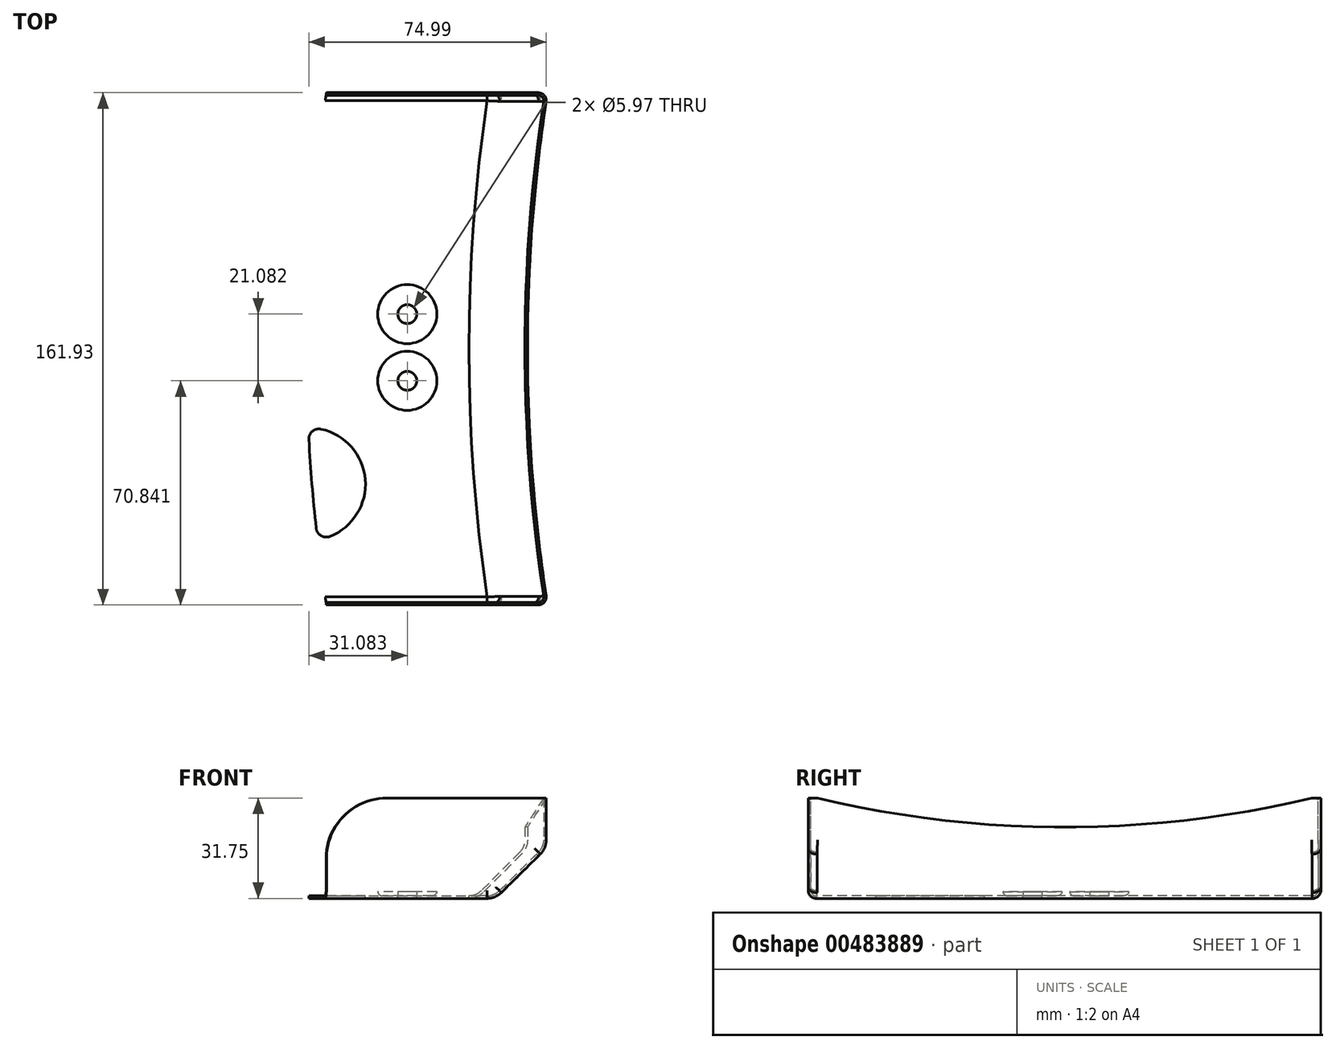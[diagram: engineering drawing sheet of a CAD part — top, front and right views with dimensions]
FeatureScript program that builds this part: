
annotation { "Feature Type Name" : "Feature", "Feature Type Description" : "" }
export const myFeature = defineFeature(function(context is Context, id is Id, definition is map)
    precondition{}
    {
        {
            var Q0;
            Q0=qCreatedBy(makeId("Top.planeOp"),FACE);
            var sketch = newSketch(context, id + "F0", { "sketchPlane" : qUnion([Q0])});
            skLineSegment(sketch, "E0.bottom", {"start": v(0, 0) * mm, "end": v(69.85, 0) * mm});
            skLineSegment(sketch, "E0.top", {"start": v(0, 161.93) * mm, "end": v(69.85, 161.93) * mm});
            skLineSegment(sketch, "E0.left", {"start": v(0, 0) * mm, "end": v(0, 161.93) * mm, "construction": true});
            skLineSegment(sketch, "E0.right", {"start": v(69.85, 0) * mm, "end": v(69.85, 161.93) * mm, "construction": true});
            skArc(sketch, "E1", {"start": v(0, 161.92) * mm, "mid": v(-6.35, 80.96) * mm, "end": v(0, 0) * mm});
            skArc(sketch, "E2", {"start": v(69.85, 161.92) * mm, "mid": v(63.5, 80.96) * mm, "end": v(69.85, 0) * mm});
            skSolve(sketch);
        }
        {
            var Q0;
            Q0=makeQuery(id+"F0.imprint","IMPRINT",FACE,{"disambiguationData":[TD([[makeQuery(id+"F0.imprint","IMPRINT",EDGE,{"derivedFrom":sQuery(id+"F0.wireOp",EDGE,"E0.bottom")}),1.0]])]});
            var Q1;
            Q1 = qBodyType(qCreatedBy(id + "F0" ,EDGE), BodyType.WIRE);
            extrude(context, id + "F1", {"entities" : qUnion([Q0]), "surfaceEntities" : qUnion([Q1]), "depth" : 31.75 * mm});
        }
        {
            var Q0;
            Q0=makeQuery(id+"F1.opExtrude","CAP_EDGE",EDGE,{"disambiguationData":[OSD([sQuery(id+"F0.wireOp",EDGE,"E2")])],"isStart":true});
            chamfer(context, id + "F2", {"entities" : qUnion([Q0]), "width" : 15.88 * mm, "tangentPropagation" : true});
        }
        {
            var Q0;
            Q0=makeQuery(id+"F1.opExtrude","CAP_EDGE",EDGE,{"disambiguationData":[OSD([sQuery(id+"F0.wireOp",EDGE,"E1")])],"isStart":false});
            fillet(context, id + "F3", {"entities" : qUnion([Q0]), "radius" : 19.05 * mm, "tangentPropagation" : true, "allowEdgeOverflow" : false});
        }
        {
            var Q0;
            {var subQ0=sQuery(id+"F0.wireOp",EDGE,"E2");Q0=makeQuery(id+"F2.opChamfer","BLEND_EDGE",EDGE,{"blendedFrom":[makeQuery(id+"F1.opExtrude","CAP_EDGE",EDGE,{"disambiguationData":[OSD([subQ0])],"isStart":true}),makeQuery(id+"F1.opExtrude","SWEPT_FACE",FACE,{"disambiguationData":[OSD([subQ0])]})],"blendedInto":[makeQuery(id+"F1.opExtrude","SWEPT_FACE",FACE,{"disambiguationData":[OSD([subQ0])]})]});}
            var Q1;
            {var subQ0=sQuery(id+"F0.wireOp",EDGE,"E2");Q1=makeQuery(id+"F2.opChamfer","BLEND_EDGE",EDGE,{"blendedFrom":[makeQuery(id+"F1.opExtrude","CAP_EDGE",EDGE,{"disambiguationData":[OSD([subQ0])],"isStart":true}),makeQuery(id+"F1.opExtrude","CAP_FACE",FACE,{"disambiguationData":[OSD([sQuery(id+"F0.wireOp",EDGE,"E0.bottom"),sQuery(id+"F0.wireOp",EDGE,"E0.top"),sQuery(id+"F0.wireOp",EDGE,"E1"),subQ0])],"isStart":true})],"blendedInto":[makeQuery(id+"F1.opExtrude","CAP_FACE",FACE,{"disambiguationData":[OSD([sQuery(id+"F0.wireOp",EDGE,"E0.bottom"),sQuery(id+"F0.wireOp",EDGE,"E0.top"),sQuery(id+"F0.wireOp",EDGE,"E1"),subQ0])],"isStart":true})]});}
            fillet(context, id + "F4", {"entities" : qUnion([Q0, Q1]), "radius" : 6.35 * mm, "tangentPropagation" : true, "allowEdgeOverflow" : false});
        }
        {
            var Q0;
            Q0=makeQuery(id+"F1.opExtrude","SWEPT_EDGE",EDGE,{"disambiguationData":[OSD([sQuery(id+"F0.wireOp",EDGE,"E0.top"),sQuery(id+"F0.wireOp",EDGE,"E2")])]});
            var Q1;
            {var subQ0=sQuery(id+"F0.wireOp",EDGE,"E2");Q1=makeQuery(id+"F4.opFillet","BLEND_EDGE",EDGE,{"blendedFrom":[makeQuery(id+"F2.opChamfer","BLEND_EDGE",EDGE,{"blendedFrom":[makeQuery(id+"F1.opExtrude","CAP_EDGE",EDGE,{"disambiguationData":[OSD([subQ0])],"isStart":true}),makeQuery(id+"F1.opExtrude","SWEPT_FACE",FACE,{"disambiguationData":[OSD([subQ0])]})],"blendedInto":[makeQuery(id+"F1.opExtrude","SWEPT_FACE",FACE,{"disambiguationData":[OSD([subQ0])]})]}),makeQuery(id+"F1.opExtrude","SWEPT_FACE",FACE,{"disambiguationData":[OSD([sQuery(id+"F0.wireOp",EDGE,"E0.bottom")])]})],"blendedInto":[makeQuery(id+"F1.opExtrude","SWEPT_FACE",FACE,{"disambiguationData":[OSD([sQuery(id+"F0.wireOp",EDGE,"E0.bottom")])]})]});}
            var Q2;
            Q2=makeQuery(id+"F1.opExtrude","SWEPT_EDGE",EDGE,{"disambiguationData":[OSD([sQuery(id+"F0.wireOp",EDGE,"E0.bottom"),sQuery(id+"F0.wireOp",EDGE,"E2")])]});
            var Q3;
            Q3=makeQuery(id+"F2.opChamfer","BLEND_EDGE",EDGE,{"blendedFrom":[makeQuery(id+"F1.opExtrude","CAP_EDGE",EDGE,{"disambiguationData":[OSD([sQuery(id+"F0.wireOp",EDGE,"E2")])],"isStart":true}),makeQuery(id+"F1.opExtrude","SWEPT_FACE",FACE,{"disambiguationData":[OSD([sQuery(id+"F0.wireOp",EDGE,"E0.top")])]})],"blendedInto":[makeQuery(id+"F1.opExtrude","SWEPT_FACE",FACE,{"disambiguationData":[OSD([sQuery(id+"F0.wireOp",EDGE,"E0.top")])]})]});
            var Q4;
            Q4=makeQuery(id+"F2.opChamfer","BLEND_EDGE",EDGE,{"blendedFrom":[makeQuery(id+"F1.opExtrude","CAP_EDGE",EDGE,{"disambiguationData":[OSD([sQuery(id+"F0.wireOp",EDGE,"E2")])],"isStart":true}),makeQuery(id+"F1.opExtrude","SWEPT_FACE",FACE,{"disambiguationData":[OSD([sQuery(id+"F0.wireOp",EDGE,"E0.bottom")])]})],"blendedInto":[makeQuery(id+"F1.opExtrude","SWEPT_FACE",FACE,{"disambiguationData":[OSD([sQuery(id+"F0.wireOp",EDGE,"E0.bottom")])]})]});
            var Q5;
            {var subQ0=sQuery(id+"F0.wireOp",EDGE,"E0.top");var subQ1=sQuery(id+"F0.wireOp",EDGE,"E2");Q5=makeQuery(id+"F4.opFillet","BLEND_EDGE",EDGE,{"blendedFrom":[makeQuery(id+"F2.opChamfer","BLEND_EDGE",EDGE,{"blendedFrom":[makeQuery(id+"F1.opExtrude","CAP_EDGE",EDGE,{"disambiguationData":[OSD([subQ1])],"isStart":true}),makeQuery(id+"F1.opExtrude","CAP_FACE",FACE,{"disambiguationData":[OSD([sQuery(id+"F0.wireOp",EDGE,"E0.bottom"),subQ0,sQuery(id+"F0.wireOp",EDGE,"E1"),subQ1])],"isStart":true})],"blendedInto":[makeQuery(id+"F1.opExtrude","CAP_FACE",FACE,{"disambiguationData":[OSD([sQuery(id+"F0.wireOp",EDGE,"E0.bottom"),subQ0,sQuery(id+"F0.wireOp",EDGE,"E1"),subQ1])],"isStart":true})]}),makeQuery(id+"F1.opExtrude","SWEPT_FACE",FACE,{"disambiguationData":[OSD([subQ0])]})],"blendedInto":[makeQuery(id+"F1.opExtrude","SWEPT_FACE",FACE,{"disambiguationData":[OSD([subQ0])]})]});}
            var Q6;
            Q6=makeQuery(id+"F1.opExtrude","CAP_EDGE",EDGE,{"disambiguationData":[OSD([sQuery(id+"F0.wireOp",EDGE,"E0.top")])],"isStart":true});
            var Q7;
            {var subQ0=sQuery(id+"F0.wireOp",EDGE,"E2");Q7=makeQuery(id+"F4.opFillet","BLEND_EDGE",EDGE,{"blendedFrom":[makeQuery(id+"F2.opChamfer","BLEND_EDGE",EDGE,{"blendedFrom":[makeQuery(id+"F1.opExtrude","CAP_EDGE",EDGE,{"disambiguationData":[OSD([subQ0])],"isStart":true}),makeQuery(id+"F1.opExtrude","SWEPT_FACE",FACE,{"disambiguationData":[OSD([subQ0])]})],"blendedInto":[makeQuery(id+"F1.opExtrude","SWEPT_FACE",FACE,{"disambiguationData":[OSD([subQ0])]})]}),makeQuery(id+"F1.opExtrude","SWEPT_FACE",FACE,{"disambiguationData":[OSD([sQuery(id+"F0.wireOp",EDGE,"E0.top")])]})],"blendedInto":[makeQuery(id+"F1.opExtrude","SWEPT_FACE",FACE,{"disambiguationData":[OSD([sQuery(id+"F0.wireOp",EDGE,"E0.top")])]})]});}
            var Q8;
            {var subQ0=sQuery(id+"F0.wireOp",EDGE,"E0.bottom");var subQ1=sQuery(id+"F0.wireOp",EDGE,"E2");Q8=makeQuery(id+"F4.opFillet","BLEND_EDGE",EDGE,{"blendedFrom":[makeQuery(id+"F2.opChamfer","BLEND_EDGE",EDGE,{"blendedFrom":[makeQuery(id+"F1.opExtrude","CAP_EDGE",EDGE,{"disambiguationData":[OSD([subQ1])],"isStart":true}),makeQuery(id+"F1.opExtrude","CAP_FACE",FACE,{"disambiguationData":[OSD([subQ0,sQuery(id+"F0.wireOp",EDGE,"E0.top"),sQuery(id+"F0.wireOp",EDGE,"E1"),subQ1])],"isStart":true})],"blendedInto":[makeQuery(id+"F1.opExtrude","CAP_FACE",FACE,{"disambiguationData":[OSD([subQ0,sQuery(id+"F0.wireOp",EDGE,"E0.top"),sQuery(id+"F0.wireOp",EDGE,"E1"),subQ1])],"isStart":true})]}),makeQuery(id+"F1.opExtrude","SWEPT_FACE",FACE,{"disambiguationData":[OSD([subQ0])]})],"blendedInto":[makeQuery(id+"F1.opExtrude","SWEPT_FACE",FACE,{"disambiguationData":[OSD([subQ0])]})]});}
            var Q9;
            Q9=makeQuery(id+"F1.opExtrude","CAP_EDGE",EDGE,{"disambiguationData":[OSD([sQuery(id+"F0.wireOp",EDGE,"E0.bottom")])],"isStart":true});
            fillet(context, id + "F5", {"entities" : qUnion([Q0, Q1, Q2, Q3, Q4, Q5, Q6, Q7, Q8, Q9]), "radius" : 2.54 * mm, "tangentPropagation" : true, "allowEdgeOverflow" : false});
        }
        {
            var Q0;
            Q0=makeQuery(id+"F1.opExtrude","CAP_FACE",FACE,{"disambiguationData":[OSD([sQuery(id+"F0.wireOp",EDGE,"E0.bottom"),sQuery(id+"F0.wireOp",EDGE,"E0.top"),sQuery(id+"F0.wireOp",EDGE,"E1"),sQuery(id+"F0.wireOp",EDGE,"E2")])],"isStart":false});
            shell(context, id + "F6", {"entities" : qUnion([Q0]), "thickness" : 0.81 * mm});
        }
        {
            var Q0;
            Q0=qCreatedBy(makeId("Right.planeOp"),FACE);
            var sketch = newSketch(context, id + "F7", { "sketchPlane" : qUnion([Q0])});
            skFitSpline(sketch, "E3.0", {"points": [v(0.81, 31.75) * mm, v(0.81, 25.4) * mm, v(0.81, 19.05) * mm, v(0.81, 12.7) * mm]});
            skFitSpline(sketch, "E3.1", {"points": [v(161.11, 12.7) * mm, v(161.11, 19.05) * mm, v(161.11, 25.4) * mm, v(161.11, 31.75) * mm]});
            skLineSegment(sketch, "E3.2", {"start": v(161.11, 12.7) * mm, "end": v(161.11, 2.54) * mm});
            skLineSegment(sketch, "E3.3", {"start": v(159.38, 0.81) * mm, "end": v(2.54, 0.81) * mm});
            skLineSegment(sketch, "E3.4", {"start": v(0.81, 12.7) * mm, "end": v(0.81, 2.54) * mm});
            skLineSegment(sketch, "E4", {"start": v(161.11, 31.75) * mm, "end": v(0.81, 31.75) * mm});
            skPoint(sketch, "E5.visualSharp", {"position": v(161.11, 0.81) * mm});
            skArc(sketch, "E5.filletArc", {"start": v(159.38, 0.81) * mm, "mid": v(160.6, 1.32) * mm, "end": v(161.11, 2.54) * mm});
            skPoint(sketch, "E6.visualSharp", {"position": v(0.81, 0.81) * mm});
            skArc(sketch, "E6.filletArc", {"start": v(0.81, 2.54) * mm, "mid": v(1.32, 1.32) * mm, "end": v(2.54, 0.81) * mm});
            skSolve(sketch);
        }
        {
            var Q0;
            Q0 = qSketchRegion(id + "F7", true);
            extrude(context, id + "F8", {"entities" : qUnion([Q0]), "operationType" : NewBodyOperationType.REMOVE, "oppositeDirection" : true, "depth" : 46.06 * mm, "hasSecondDirection" : true, "secondDirectionOppositeDirection" : false, "secondDirectionDepth" : 24.57 * mm});
        }
        {
            var Q0;
            Q0=qCreatedBy(makeId("Right.planeOp"),FACE);
            var sketch = newSketch(context, id + "F9", { "sketchPlane" : qUnion([Q0])});
            skLineSegment(sketch, "E7.0", {"start": v(2.8, 31.75) * mm, "end": v(2.8, 18.5) * mm, "construction": true});
            skLineSegment(sketch, "E8.0", {"start": v(159.13, 18.5) * mm, "end": v(159.13, 31.75) * mm, "construction": true});
            skArc(sketch, "E9", {"start": v(2.8, 31.75) * mm, "mid": v(80.96, 22.52) * mm, "end": v(159.13, 31.75) * mm});
            skLineSegment(sketch, "E10", {"start": v(159.13, 31.75) * mm, "end": v(2.8, 31.75) * mm});
            skSolve(sketch);
        }
        {
            var Q0;
            Q0=makeQuery(id+"F9.imprint","IMPRINT",FACE,{"disambiguationData":[TD([[makeQuery(id+"F9.imprint","IMPRINT",EDGE,{"derivedFrom":sQuery(id+"F9.wireOp",EDGE,"E9")}),1.0]])]});
            extrude(context, id + "F10", {"entities" : qUnion([Q0]), "operationType" : NewBodyOperationType.REMOVE, "endBound" : BoundingType.THROUGH_ALL, "depth" : 25.4 * mm});
        }
        {
            var Q0;
            {var subQ0=sQuery(id+"F0.wireOp",EDGE,"E2");var subQ1=sQuery(id+"F0.wireOp",EDGE,"E1");var subQ2=sQuery(id+"F0.wireOp",EDGE,"E0.top");var subQ3=sQuery(id+"F0.wireOp",EDGE,"E0.bottom");Q0=makeQuery(id+"F6.opShell","OFFSET_FACE",FACE,{"disambiguationData":[OSD([subQ3,subQ2,subQ1,subQ0]),TDD([makeQuery(id+"F1.opExtrude","CAP_FACE",FACE,{"disambiguationData":[OSD([subQ3,subQ2,subQ1,subQ0])],"isStart":true})])]});}
            var sketch = newSketch(context, id + "F11", { "sketchPlane" : qUnion([Q0])});
            skLineSegment(sketch, "E11", {"start": v(-5.95, 81.38) * mm, "end": v(45, 81.38) * mm, "construction": true});
            skFitSpline(sketch, "E12.0", {"points": [v(0.34, 0.4) * mm, v(10.8, 0.4) * mm, v(21.24, 0.4) * mm, v(31.7, 0.4) * mm], "construction": true});
            skFitSpline(sketch, "E13.0", {"points": [v(31.7, 161.53) * mm, v(21.24, 161.53) * mm, v(10.8, 161.53) * mm, v(0.34, 161.53) * mm], "construction": true});
            skLineSegment(sketch, "E14.0", {"start": v(-5.33, 106.78) * mm, "end": v(25.94, 106.78) * mm, "construction": true});
            skLineSegment(sketch, "E15.0", {"start": v(5.53, 138.53) * mm, "end": v(25.94, 138.53) * mm, "construction": true});
            skArc(sketch, "E16", {"start": v(-5.33, 106.78) * mm, "mid": v(11.36, 118.8) * mm, "end": v(5.53, 138.53) * mm});
            skArc(sketch, "E17", {"start": v(5.53, 138.53) * mm, "mid": v(-22.29, 130.32) * mm, "end": v(-5.33, 106.78) * mm});
            skArc(sketch, "E18.MirrorCS", {"start": v(5.53, 24.23) * mm, "mid": v(-22.29, 32.45) * mm, "end": v(-5.33, 55.98) * mm});
            skArc(sketch, "E19.MirrorCS", {"start": v(-5.33, 55.98) * mm, "mid": v(11.36, 43.96) * mm, "end": v(5.53, 24.23) * mm});
            skCircle(sketch, "E20", {"center": v(25.52, 91.92) * mm, "radius": 2.98 * mm});
            skCircle(sketch, "E21.MirrorC", {"center": v(25.52, 70.84) * mm, "radius": 2.98 * mm});
            skSolve(sketch);
        }
        {
            var Q0;
            {var subQ0=sQuery(id+"F11.wireOp",EDGE,"E16");Q0=makeQuery(id+"F11.imprint","IMPRINT",FACE,{"disambiguationData":[TD([[makeQuery(id+"F11.imprint","IMPRINT",EDGE,{"derivedFrom":subQ0}),1.0]])]});}
            var Q1;
            {var subQ0=sQuery(id+"F11.wireOp",EDGE,"E17");Q1=makeQuery(id+"F11.imprint","IMPRINT",FACE,{"disambiguationData":[TD([[makeQuery(id+"F11.imprint","IMPRINT",EDGE,{"derivedFrom":subQ0}),1.0]])]});}
            var Q2;
            {var subQ0=sQuery(id+"F11.wireOp",EDGE,"E18.MirrorCS");Q2=makeQuery(id+"F11.imprint","IMPRINT",FACE,{"disambiguationData":[TD([[makeQuery(id+"F11.imprint","IMPRINT",EDGE,{"derivedFrom":subQ0}),-1.0]])]});}
            var Q3;
            {var subQ0=sQuery(id+"F11.wireOp",EDGE,"E19.MirrorCS");Q3=makeQuery(id+"F11.imprint","IMPRINT",FACE,{"disambiguationData":[TD([[makeQuery(id+"F11.imprint","IMPRINT",EDGE,{"derivedFrom":subQ0}),-1.0]])]});}
            var Q4;
            {var subQ0=sQuery(id+"F11.wireOp",EDGE,"E20");var subQ1=sQuery(id+"F0.wireOp",EDGE,"E2");var subQ2=sQuery(id+"F0.wireOp",EDGE,"E1");var subQ3=sQuery(id+"F0.wireOp",EDGE,"E0.top");var subQ4=sQuery(id+"F0.wireOp",EDGE,"E0.bottom");var subQ5=makeQuery(id+"F1.opExtrude","CAP_FACE",FACE,{"disambiguationData":[OSD([subQ4,subQ3,subQ2,subQ1])],"isStart":true});var subQ6=makeQuery(id+"F6.opShell","OFFSET_EDGE",EDGE,{"disambiguationData":[OSD([subQ4,subQ3,subQ2,subQ1]),TDD([makeQuery(id+"F4.opFillet","BLEND_EDGE",EDGE,{"blendedFrom":[makeQuery(id+"F2.opChamfer","BLEND_EDGE",EDGE,{"blendedFrom":[makeQuery(id+"F1.opExtrude","CAP_EDGE",EDGE,{"disambiguationData":[OSD([subQ1])],"isStart":true}),subQ5],"blendedInto":[subQ5]}),subQ5],"blendedInto":[subQ5]})])]});var subQ7=makeQuery(id+"F11.imprint","INTERSECT",VERTEX,{"disambiguationData":[OD(0.0)],"derivedFrom":[subQ6,subQ0]});Q4=makeQuery(id+"F11.imprint","IMPRINT",FACE,{"disambiguationData":[TD([[makeQuery(id+"F11.imprint","IMPRINT",EDGE,{"disambiguationData":[TD([[subQ7,-1.0]])],"derivedFrom":subQ0}),1.0]])]});}
            var Q5;
            {var subQ0=sQuery(id+"F11.wireOp",EDGE,"E21.MirrorC");var subQ1=sQuery(id+"F0.wireOp",EDGE,"E2");var subQ2=sQuery(id+"F0.wireOp",EDGE,"E1");var subQ3=sQuery(id+"F0.wireOp",EDGE,"E0.top");var subQ4=sQuery(id+"F0.wireOp",EDGE,"E0.bottom");var subQ5=makeQuery(id+"F1.opExtrude","CAP_FACE",FACE,{"disambiguationData":[OSD([subQ4,subQ3,subQ2,subQ1])],"isStart":true});var subQ6=makeQuery(id+"F6.opShell","OFFSET_EDGE",EDGE,{"disambiguationData":[OSD([subQ4,subQ3,subQ2,subQ1]),TDD([makeQuery(id+"F4.opFillet","BLEND_EDGE",EDGE,{"blendedFrom":[makeQuery(id+"F2.opChamfer","BLEND_EDGE",EDGE,{"blendedFrom":[makeQuery(id+"F1.opExtrude","CAP_EDGE",EDGE,{"disambiguationData":[OSD([subQ1])],"isStart":true}),subQ5],"blendedInto":[subQ5]}),subQ5],"blendedInto":[subQ5]})])]});var subQ7=makeQuery(id+"F11.imprint","INTERSECT",VERTEX,{"disambiguationData":[OD(0.0)],"derivedFrom":[subQ6,subQ0]});Q5=makeQuery(id+"F11.imprint","IMPRINT",FACE,{"disambiguationData":[TD([[makeQuery(id+"F11.imprint","IMPRINT",EDGE,{"disambiguationData":[TD([[subQ7,-1.0]])],"derivedFrom":subQ0}),-1.0]])]});}
            extrude(context, id + "F12", {"entities" : qUnion([Q0, Q1, Q2, Q3, Q4, Q5]), "operationType" : NewBodyOperationType.REMOVE, "oppositeDirection" : true, "depth" : 25.4 * mm});
        }
        {
            var Q0;
            {var subQ0=sQuery(id+"F11.wireOp",EDGE,"E17");var subQ1=sQuery(id+"F7.wireOp",EDGE,"E3.3");var subQ2=sQuery(id+"F0.wireOp",EDGE,"E1");Q0=makeQuery(id+"F12.boolean.opBoolean","COPY",EDGE,{"derivedFrom":makeQuery(id+"F12.opExtrude","SWEPT_EDGE",EDGE,{"disambiguationData":[OSD([subQ2,subQ1,subQ0]),TDD([makeQuery(id+"F11.imprint","INTERSECT",VERTEX,{"disambiguationData":[OD(1.0)],"derivedFrom":[makeQuery(id+"F8.boolean.opBoolean","INTERSECT",EDGE,{"derivedFrom":[makeQuery(id+"F1.opExtrude","SWEPT_FACE",FACE,{"disambiguationData":[OSD([subQ2])]}),makeQuery(id+"F8.opExtrude","SWEPT_FACE",FACE,{"disambiguationData":[OSD([subQ1])]})]}),subQ0]})])]})});}
            var Q1;
            {var subQ0=sQuery(id+"F11.wireOp",EDGE,"E17");var subQ1=sQuery(id+"F7.wireOp",EDGE,"E3.3");var subQ2=sQuery(id+"F0.wireOp",EDGE,"E1");Q1=makeQuery(id+"F12.boolean.opBoolean","COPY",EDGE,{"derivedFrom":makeQuery(id+"F12.opExtrude","SWEPT_EDGE",EDGE,{"disambiguationData":[OSD([subQ2,subQ1,subQ0]),TDD([makeQuery(id+"F11.imprint","INTERSECT",VERTEX,{"disambiguationData":[OD(0.0)],"derivedFrom":[makeQuery(id+"F8.boolean.opBoolean","INTERSECT",EDGE,{"derivedFrom":[makeQuery(id+"F1.opExtrude","SWEPT_FACE",FACE,{"disambiguationData":[OSD([subQ2])]}),makeQuery(id+"F8.opExtrude","SWEPT_FACE",FACE,{"disambiguationData":[OSD([subQ1])]})]}),subQ0]})])]})});}
            var Q2;
            {var subQ0=sQuery(id+"F11.wireOp",EDGE,"E18.MirrorCS");var subQ1=sQuery(id+"F7.wireOp",EDGE,"E3.3");var subQ2=sQuery(id+"F0.wireOp",EDGE,"E1");Q2=makeQuery(id+"F12.boolean.opBoolean","COPY",EDGE,{"derivedFrom":makeQuery(id+"F12.opExtrude","SWEPT_EDGE",EDGE,{"disambiguationData":[OSD([subQ2,subQ1,subQ0]),TDD([makeQuery(id+"F11.imprint","INTERSECT",VERTEX,{"disambiguationData":[OD(1.0)],"derivedFrom":[makeQuery(id+"F8.boolean.opBoolean","INTERSECT",EDGE,{"derivedFrom":[makeQuery(id+"F1.opExtrude","SWEPT_FACE",FACE,{"disambiguationData":[OSD([subQ2])]}),makeQuery(id+"F8.opExtrude","SWEPT_FACE",FACE,{"disambiguationData":[OSD([subQ1])]})]}),subQ0]})])]})});}
            var Q3;
            {var subQ0=sQuery(id+"F11.wireOp",EDGE,"E18.MirrorCS");var subQ1=sQuery(id+"F7.wireOp",EDGE,"E3.3");var subQ2=sQuery(id+"F0.wireOp",EDGE,"E1");Q3=makeQuery(id+"F12.boolean.opBoolean","COPY",EDGE,{"derivedFrom":makeQuery(id+"F12.opExtrude","SWEPT_EDGE",EDGE,{"disambiguationData":[OSD([subQ2,subQ1,subQ0]),TDD([makeQuery(id+"F11.imprint","INTERSECT",VERTEX,{"disambiguationData":[OD(0.0)],"derivedFrom":[makeQuery(id+"F8.boolean.opBoolean","INTERSECT",EDGE,{"derivedFrom":[makeQuery(id+"F1.opExtrude","SWEPT_FACE",FACE,{"disambiguationData":[OSD([subQ2])]}),makeQuery(id+"F8.opExtrude","SWEPT_FACE",FACE,{"disambiguationData":[OSD([subQ1])]})]}),subQ0]})])]})});}
            fillet(context, id + "F13", {"entities" : qUnion([Q0, Q1, Q2, Q3]), "radius" : 3.17 * mm, "tangentPropagation" : true, "allowEdgeOverflow" : false});
        }
        {
            var Q0;
            {var subQ0=sQuery(id+"F0.wireOp",EDGE,"E2");var subQ1=sQuery(id+"F0.wireOp",EDGE,"E1");var subQ2=sQuery(id+"F0.wireOp",EDGE,"E0.top");var subQ3=sQuery(id+"F0.wireOp",EDGE,"E0.bottom");Q0=makeQuery(id+"F6.opShell","OFFSET_FACE",FACE,{"disambiguationData":[OSD([subQ3,subQ2,subQ1,subQ0]),TDD([makeQuery(id+"F1.opExtrude","CAP_FACE",FACE,{"disambiguationData":[OSD([subQ3,subQ2,subQ1,subQ0])],"isStart":true})])]});}
            var sketch = newSketch(context, id + "F14", { "sketchPlane" : qUnion([Q0])});
            skCircle(sketch, "E22.0", {"center": v(25.52, 91.92) * mm, "radius": 2.98 * mm});
            skCircle(sketch, "E22.1", {"center": v(25.52, 70.84) * mm, "radius": 2.98 * mm});
            skCircle(sketch, "E23.0", {"center": v(25.52, 91.92) * mm, "radius": 9.33 * mm});
            skCircle(sketch, "E24.0", {"center": v(25.52, 70.84) * mm, "radius": 9.33 * mm});
            skSolve(sketch);
        }
        {
            var Q0;
            Q0 = qSketchRegion(id + "F14", true);
            extrude(context, id + "F15", {"entities" : qUnion([Q0]), "operationType" : NewBodyOperationType.ADD, "depth" : 1.35 * mm});
        }
        {
            var Q0;
            Q0=makeQuery(id+"F15.opExtrude","CAP_EDGE",EDGE,{"disambiguationData":[OSD([sQuery(id+"F14.wireOp",EDGE,"E23.0")])],"isStart":true});
            var Q1;
            Q1=makeQuery(id+"F15.opExtrude","CAP_EDGE",EDGE,{"disambiguationData":[OSD([sQuery(id+"F14.wireOp",EDGE,"E24.0")])],"isStart":true});
            fillet(context, id + "F16", {"entities" : qUnion([Q0, Q1]), "radius" : 1.52 * mm, "tangentPropagation" : true, "allowEdgeOverflow" : false});
        }
    });
